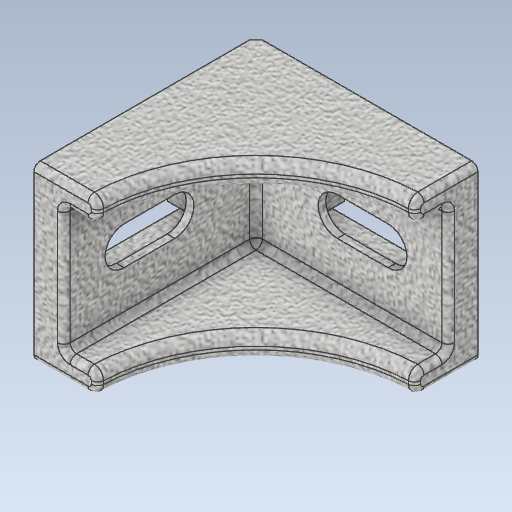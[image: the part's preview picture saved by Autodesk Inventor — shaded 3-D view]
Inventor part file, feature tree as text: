
AUTODESK INVENTOR PART (.ipt)
format: ipt  version: 2020.2 (Build 242310000, 310)  size: 563,200 bytes
history: native  units: mm
features: extrude x12, sketch x12, fillet x4, mirror x3, pattern_circular x1, chamfer x1, projected_geometry x1
ambient origin geometry x8: Origin, YZ Plane, XZ Plane, XY Plane, X Axis, Y Axis, Z Axis, Center Point
bodies: Solid1 (feature_tree)
feature tree (34):
  extrude  "Extrusion1"  Depth=27.0mm
  extrude  "Extrusion2"  Depth=4.7mm
  extrude  "Extrusion3"  Depth=30.3mm
  extrude  "Extrusion4"  Depth=10.0mm TaperAngle=0.0deg
  fillet  "Fillet1"  Radius=10.0mm
  mirror  "Mirror1"
  extrude  "Extrusion5"  Depth=10.0mm TaperAngle=0.0deg
  pattern_circular  "Circular Pattern1"  Count=2 Angle=90.0deg
  extrude  "Extrusion6"  Depth=3.0mm
  extrude  "Extrusion7"  Depth=1.0mm
  mirror  "Mirror2"
  extrude  "Extrusion8"  Depth=1.0mm
  mirror  "Mirror3"
  extrude  "Extrusion9"  Depth=1.0mm TaperAngle=0.0deg
  extrude  "Extrusion10"  Depth=1.0mm
  extrude  "Extrusion11"  Depth=1.0mm
  extrude  "Extrusion12"  Depth=1.0mm
  fillet  "Fillet2"  Radius=3.3mm
  fillet  "Fillet3"  Radius=3.5mm
  fillet  "Fillet4"  Radius=1.0mm
  chamfer  "Chamfer1"  Distance=17.0mm
  sketch  "Sketch1"  dims[d0=35.0mm d1=27.0mm]
  sketch  "Sketch2"  dims[d2=4.7mm d3=0.0mm d4=4.7mm]
  sketch  "Sketch3"  dims[d5=30.3mm d6=0.0mm d7=30.3mm]
  sketch  "Sketch4"  dims[d8=3.5mm d9=30.3mm d10=0.0mm d11=10.0mm]
  sketch  "Sketch5"  dims[d12=10.0mm d13=4.0mm d14=0.0mm]
  sketch  "Sketch6"  dims[d15=1.5mm]
  projected_geometry  "Projected Loop1"
  sketch  "Sketch7"  dims[d16=6.5mm]
  sketch  "Sketch8"  dims[d17=7.0mm]
  sketch  "Sketch9"  dims[d18=3.0mm]
  sketch  "Sketch10"  dims[d19=5.0mm d20=0.0mm d21=20.0mm d22=90.0deg]
  sketch  "Sketch11"  dims[d24=5.0mm d25=0.0mm d26=3.0mm]
  sketch  "Sketch12"  dims[d27=1.65mm d28=28.0mm d29=3.3mm d30=3.5mm d31=0.0mm d32=3.0mm d33=1.65mm d34=28.0mm d35=3.3mm d36=3.5mm d37=0.0mm d38=1.0mm d39=17.0mm d40=8.0mm d41=3.5mm d42=0.0mm d43=2.0mm d44=0.0mm d45=1.0mm d46=17.0mm d47=8.0mm d48=3.5mm d49=0.0mm d50=2.0mm d51=8.0mm d52=2.0mm d53=8.0mm d54=2.0mm d55=0.0mm d56=1.5mm d57=1.0mm d58=1.0mm d59=1.0mm d60=2.0mm d61=45.0deg]
